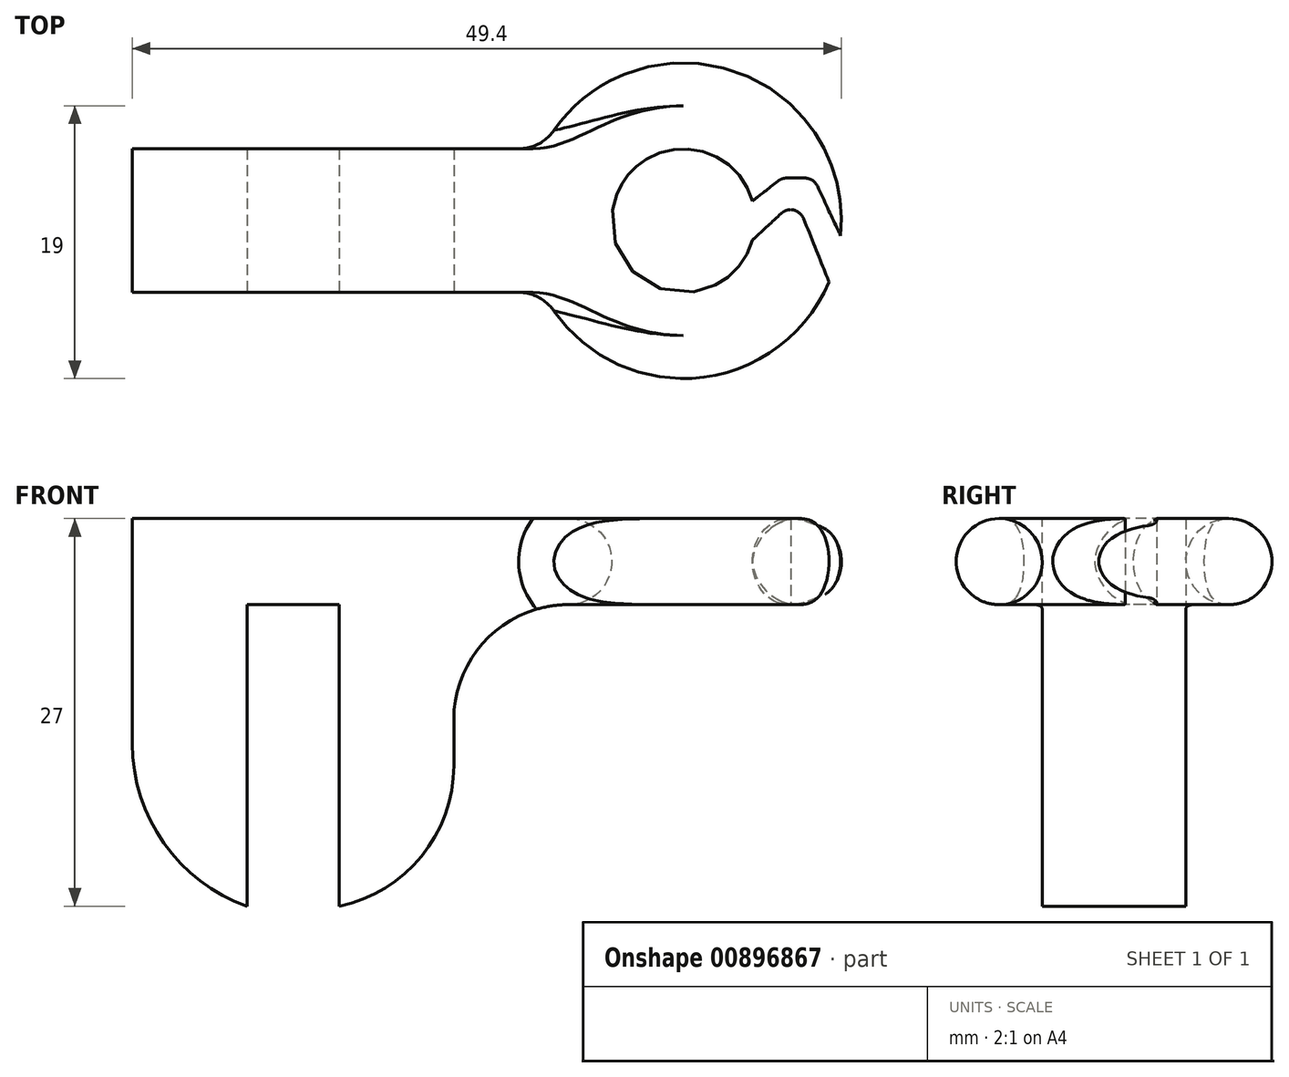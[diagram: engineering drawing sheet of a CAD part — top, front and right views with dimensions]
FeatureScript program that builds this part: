
annotation { "Feature Type Name" : "Feature", "Feature Type Description" : "" }
export const myFeature = defineFeature(function(context is Context, id is Id, definition is map)
    precondition{}
    {
        {
            var Q0;
            Q0=qCreatedBy(makeId("Front.planeOp"),FACE);
            var sketch = newSketch(context, id + "F0", { "sketchPlane" : qUnion([Q0])});
            skLineSegment(sketch, "E0", {"start": v(0, 0) * mm, "end": v(8, 0) * mm, "construction": true});
            skCircle(sketch, "E1", {"center": v(8, 0) * mm, "radius": 3 * mm});
            skLineSegment(sketch, "E2", {"start": v(0, 0) * mm, "end": v(0, 3.74) * mm, "construction": true});
            skSolve(sketch);
        }
        {
            var Q0;
            Q0=makeQuery(id+"F0.imprint","IMPRINT",FACE,{"disambiguationData":[TD([[makeQuery(id+"F0.imprint","IMPRINT",EDGE,{"derivedFrom":sQuery(id+"F0.wireOp",EDGE,"E1")}),1.0]])]});
            var Q1;
            Q1=sQuery(id+"F0.wireOp",EDGE,"E2");
            revolve(context, id + "F1", {"surfaceOperationType" : NewSurfaceOperationType.NEW, "entities" : qUnion([Q0]), "axis" : qUnion([Q1]), "revolveType" : RevolveType.FULL});
        }
        {
            var Q0;
            Q0=qCreatedBy(makeId("Top.planeOp"),FACE);
            var sketch = newSketch(context, id + "F2", { "sketchPlane" : qUnion([Q0])});
            skLineSegment(sketch, "E3", {"start": v(0, 0) * mm, "end": v(-8, 0) * mm, "construction": true});
            skLineSegment(sketch, "E4", {"start": v(-8, 0) * mm, "end": v(-8, 5) * mm});
            skLineSegment(sketch, "E5", {"start": v(-8, 5) * mm, "end": v(-38.4, 5) * mm});
            skLineSegment(sketch, "E6", {"start": v(-38.4, 5) * mm, "end": v(-38.4, -5) * mm});
            skLineSegment(sketch, "E7", {"start": v(-38.4, -5) * mm, "end": v(-8, -5) * mm});
            skLineSegment(sketch, "E8", {"start": v(-8, -5) * mm, "end": v(-8, 0) * mm});
            skLineSegment(sketch, "E9", {"start": v(-30.4, 5) * mm, "end": v(-30.4, -5) * mm});
            skLineSegment(sketch, "E10", {"start": v(-24, 5) * mm, "end": v(-24, -5) * mm});
            skLineSegment(sketch, "E11", {"start": v(-16, 5) * mm, "end": v(-16, -5) * mm});
            skCircle(sketch, "E12", {"center": v(0, 0) * mm, "radius": 8 * mm});
            skLineSegment(sketch, "E13", {"start": v(-8, 5) * mm, "end": v(-6.24, 5) * mm});
            skLineSegment(sketch, "E14", {"start": v(-8, -5) * mm, "end": v(-6.24, -5) * mm});
            skSolve(sketch);
        }
        {
            var Q0;
            {var subQ0=sQuery(id+"F2.wireOp",EDGE,"E6");Q0=makeQuery(id+"F2.imprint","IMPRINT",FACE,{"disambiguationData":[TD([[makeQuery(id+"F2.imprint","IMPRINT",EDGE,{"derivedFrom":subQ0}),1.0]])]});}
            var Q1;
            {var subQ0=sQuery(id+"F2.wireOp",EDGE,"E9");Q1=makeQuery(id+"F2.imprint","IMPRINT",FACE,{"disambiguationData":[TD([[makeQuery(id+"F2.imprint","IMPRINT",EDGE,{"derivedFrom":subQ0}),1.0]])]});}
            var Q2;
            {var subQ0=sQuery(id+"F2.wireOp",EDGE,"E10");Q2=makeQuery(id+"F2.imprint","IMPRINT",FACE,{"disambiguationData":[TD([[makeQuery(id+"F2.imprint","IMPRINT",EDGE,{"derivedFrom":subQ0}),1.0]])]});}
            var Q3;
            {var subQ4=sQuery(id+"F2.wireOp",EDGE,"E4");Q3=makeQuery(id+"F2.imprint","IMPRINT",FACE,{"disambiguationData":[TD([[makeQuery(id+"F2.imprint","IMPRINT",EDGE,{"derivedFrom":subQ4}),1.0]])]});}
            var Q4;
            {var subQ0=sQuery(id+"F2.wireOp",EDGE,"E4");Q4=makeQuery(id+"F2.imprint","IMPRINT",FACE,{"disambiguationData":[TD([[makeQuery(id+"F2.imprint","IMPRINT",EDGE,{"derivedFrom":subQ0}),-1.0]])]});}
            var Q5;
            {var subQ0=sQuery(id+"F2.wireOp",EDGE,"E8");Q5=makeQuery(id+"F2.imprint","IMPRINT",FACE,{"disambiguationData":[TD([[makeQuery(id+"F2.imprint","IMPRINT",EDGE,{"derivedFrom":subQ0}),-1.0]])]});}
            extrude(context, id + "F3", {"entities" : qUnion([Q0, Q1, Q2, Q3, Q4, Q5]), "operationType" : NewBodyOperationType.ADD, "endBound" : BoundingType.SYMMETRIC, "depth" : 6 * mm, "offsetDistance" : 25 * mm});
        }
        {
            var Q0;
            {var subQ0=sQuery(id+"F2.wireOp",EDGE,"E6");Q0=makeQuery(id+"F2.imprint","IMPRINT",FACE,{"disambiguationData":[TD([[makeQuery(id+"F2.imprint","IMPRINT",EDGE,{"derivedFrom":subQ0}),1.0]])]});}
            var Q1;
            {var subQ0=sQuery(id+"F2.wireOp",EDGE,"E10");Q1=makeQuery(id+"F2.imprint","IMPRINT",FACE,{"disambiguationData":[TD([[makeQuery(id+"F2.imprint","IMPRINT",EDGE,{"derivedFrom":subQ0}),1.0]])]});}
            extrude(context, id + "F4", {"entities" : qUnion([Q0, Q1]), "operationType" : NewBodyOperationType.ADD, "oppositeDirection" : true, "depth" : 24 * mm, "offsetDistance" : 25 * mm});
        }
        {
            var Q0;
            Q0=makeQuery(id+"F4.boolean.opBoolean","INTERSECT",EDGE,{"derivedFrom":[makeQuery(id+"F3.opExtrude","CAP_FACE",FACE,{"disambiguationData":[OSD([sQuery(id+"F2.wireOp",EDGE,"E4"),sQuery(id+"F2.wireOp",EDGE,"E5"),sQuery(id+"F2.wireOp",EDGE,"E6"),sQuery(id+"F2.wireOp",EDGE,"E7"),sQuery(id+"F2.wireOp",EDGE,"E8")])],"isStart":true}),makeQuery(id+"F4.opExtrude","SWEPT_FACE",FACE,{"disambiguationData":[OSD([sQuery(id+"F2.wireOp",EDGE,"E11")])]})]});
            fillet(context, id + "F5", {"entities" : qUnion([Q0]), "radius" : 8 * mm, "tangentPropagation" : true, "allowEdgeOverflow" : false});
        }
        {
            var Q0;
            Q0=makeQuery(id+"F4.opExtrude","CAP_EDGE",EDGE,{"disambiguationData":[OSD([sQuery(id+"F2.wireOp",EDGE,"E11")])],"isStart":false});
            fillet(context, id + "F6", {"entities" : qUnion([Q0]), "radius" : 10 * mm, "tangentPropagation" : true, "allowEdgeOverflow" : false});
        }
        {
            var Q0;
            Q0=makeQuery(id+"F4.opExtrude","CAP_EDGE",EDGE,{"disambiguationData":[OSD([sQuery(id+"F2.wireOp",EDGE,"E6")])],"isStart":false});
            fillet(context, id + "F7", {"entities" : qUnion([Q0]), "radius" : 12 * mm, "tangentPropagation" : true, "allowEdgeOverflow" : false});
        }
        {
            var Q0;
            Q0=makeQuery(id+"F3.boolean.opBoolean","INTERSECT",EDGE,{"derivedFrom":[makeQuery(id+"F1.opRevolve","SWEPT_FACE",FACE,{"disambiguationData":[OSD([sQuery(id+"F0.wireOp",EDGE,"E1")])]}),makeQuery(id+"F3.opExtrude","SWEPT_FACE",FACE,{"disambiguationData":[OSD([sQuery(id+"F2.wireOp",EDGE,"E7"),sQuery(id+"F2.wireOp",EDGE,"E14")])]})]});
            var Q1;
            Q1=makeQuery(id+"F3.boolean.opBoolean","INTERSECT",EDGE,{"derivedFrom":[makeQuery(id+"F1.opRevolve","SWEPT_FACE",FACE,{"disambiguationData":[OSD([sQuery(id+"F0.wireOp",EDGE,"E1")])]}),makeQuery(id+"F3.opExtrude","SWEPT_FACE",FACE,{"disambiguationData":[OSD([sQuery(id+"F2.wireOp",EDGE,"E5"),sQuery(id+"F2.wireOp",EDGE,"E13")])]})]});
            fillet(context, id + "F8", {"entities" : qUnion([Q0, Q1]), "radius" : 3 * mm, "tangentPropagation" : true, "allowEdgeOverflow" : false});
        }
        {
            var Q0;
            Q0=qCreatedBy(makeId("Top.planeOp"),FACE);
            var sketch = newSketch(context, id + "F9", { "sketchPlane" : qUnion([Q0])});
            skLineSegment(sketch, "E15", {"start": v(4.17, -1.94) * mm, "end": v(7.11, 0.77) * mm});
            skLineSegment(sketch, "E16", {"start": v(7.11, 0.77) * mm, "end": v(8.12, 0.77) * mm});
            skLineSegment(sketch, "E17", {"start": v(8.12, 0.77) * mm, "end": v(10.84, -6.04) * mm});
            skLineSegment(sketch, "E18", {"start": v(10.84, -6.04) * mm, "end": v(12.85, -5.15) * mm});
            skLineSegment(sketch, "E19", {"start": v(12.85, -5.15) * mm, "end": v(9.07, 2.97) * mm});
            skLineSegment(sketch, "E20", {"start": v(9.07, 2.97) * mm, "end": v(6.86, 2.97) * mm});
            skLineSegment(sketch, "E21", {"start": v(6.86, 2.97) * mm, "end": v(2.68, -0.32) * mm});
            skLineSegment(sketch, "E22", {"start": v(2.68, -0.32) * mm, "end": v(4.17, -1.94) * mm});
            skSolve(sketch);
        }
        {
            var Q0;
            Q0=makeQuery(id+"F9.imprint","IMPRINT",FACE,{"disambiguationData":[TD([[makeQuery(id+"F9.imprint","IMPRINT",EDGE,{"derivedFrom":sQuery(id+"F9.wireOp",EDGE,"E15")}),1.0]])]});
            extrude(context, id + "F10", {"entities" : qUnion([Q0]), "operationType" : NewBodyOperationType.REMOVE, "endBound" : BoundingType.SYMMETRIC, "depth" : 13.8 * mm, "offsetDistance" : 25 * mm});
        }
        {
            var Q0;
            Q0=makeQuery(id+"F10.boolean.opBoolean","COPY",EDGE,{"derivedFrom":makeQuery(id+"F10.opExtrude","SWEPT_EDGE",EDGE,{"disambiguationData":[OSD([sQuery(id+"F9.wireOp",EDGE,"E20"),sQuery(id+"F9.wireOp",EDGE,"E21")])]})});
            var Q1;
            Q1=makeQuery(id+"F10.boolean.opBoolean","COPY",EDGE,{"derivedFrom":makeQuery(id+"F10.opExtrude","SWEPT_EDGE",EDGE,{"disambiguationData":[OSD([sQuery(id+"F9.wireOp",EDGE,"E19"),sQuery(id+"F9.wireOp",EDGE,"E20")])]})});
            var Q2;
            Q2=makeQuery(id+"F10.boolean.opBoolean","COPY",EDGE,{"derivedFrom":makeQuery(id+"F10.opExtrude","SWEPT_EDGE",EDGE,{"disambiguationData":[OSD([sQuery(id+"F9.wireOp",EDGE,"E16"),sQuery(id+"F9.wireOp",EDGE,"E17")])]})});
            var Q3;
            Q3=makeQuery(id+"F10.boolean.opBoolean","COPY",EDGE,{"derivedFrom":makeQuery(id+"F10.opExtrude","SWEPT_EDGE",EDGE,{"disambiguationData":[OSD([sQuery(id+"F9.wireOp",EDGE,"E15"),sQuery(id+"F9.wireOp",EDGE,"E16")])]})});
            fillet(context, id + "F11", {"entities" : qUnion([Q0, Q1, Q2, Q3]), "radius" : 1 * mm, "tangentPropagation" : true, "allowEdgeOverflow" : false});
        }
    });
